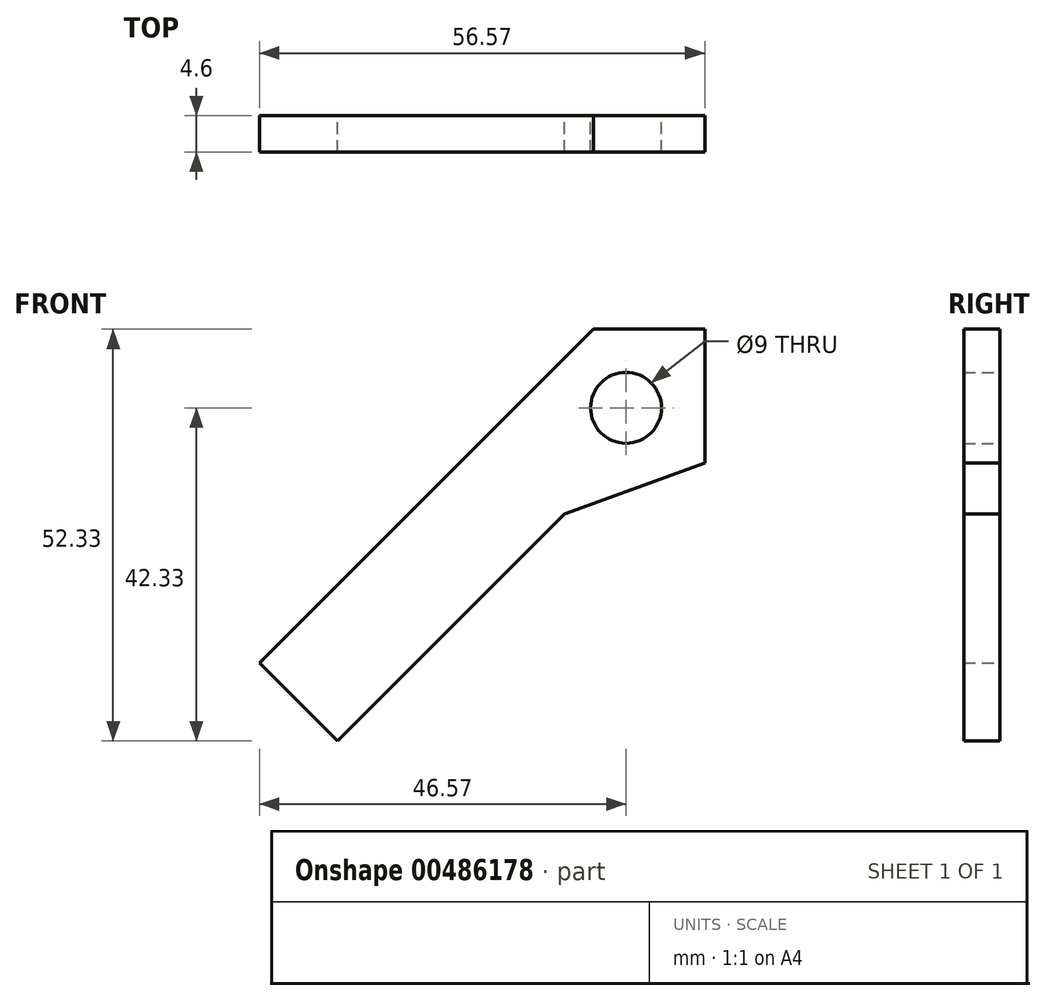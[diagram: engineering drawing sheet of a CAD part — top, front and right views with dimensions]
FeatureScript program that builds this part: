
annotation { "Feature Type Name" : "Feature", "Feature Type Description" : "" }
export const myFeature = defineFeature(function(context is Context, id is Id, definition is map)
    precondition{}
    {
        {
            var Q0;
            Q0=qCreatedBy(makeId("Front.planeOp"),FACE);
            var sketch = newSketch(context, id + "F0", { "sketchPlane" : qUnion([Q0])});
            skLineSegment(sketch, "E0", {"start": v(-4.14, 10) * mm, "end": v(10, 10) * mm});
            skLineSegment(sketch, "E1", {"start": v(10, 10) * mm, "end": v(10, -7) * mm});
            skLineSegment(sketch, "E2", {"start": v(-7.84, -13.5) * mm, "end": v(-36.67, -42.33) * mm});
            skLineSegment(sketch, "E3", {"start": v(-36.67, -42.33) * mm, "end": v(-46.57, -32.43) * mm});
            skLineSegment(sketch, "E4", {"start": v(-46.57, -32.43) * mm, "end": v(-4.14, 10) * mm});
            skCircle(sketch, "E5", {"center": v(0, 0) * mm, "radius": 4.5 * mm});
            skLineSegment(sketch, "E6", {"start": v(10, -7) * mm, "end": v(-7.84, -13.5) * mm});
            skSolve(sketch);
        }
        {
            var Q0;
            Q0 = qSketchRegion(id + "F0", true);
            extrude(context, id + "F1", {"entities" : qUnion([Q0]), "depth" : 4.6 * mm});
        }
    });
